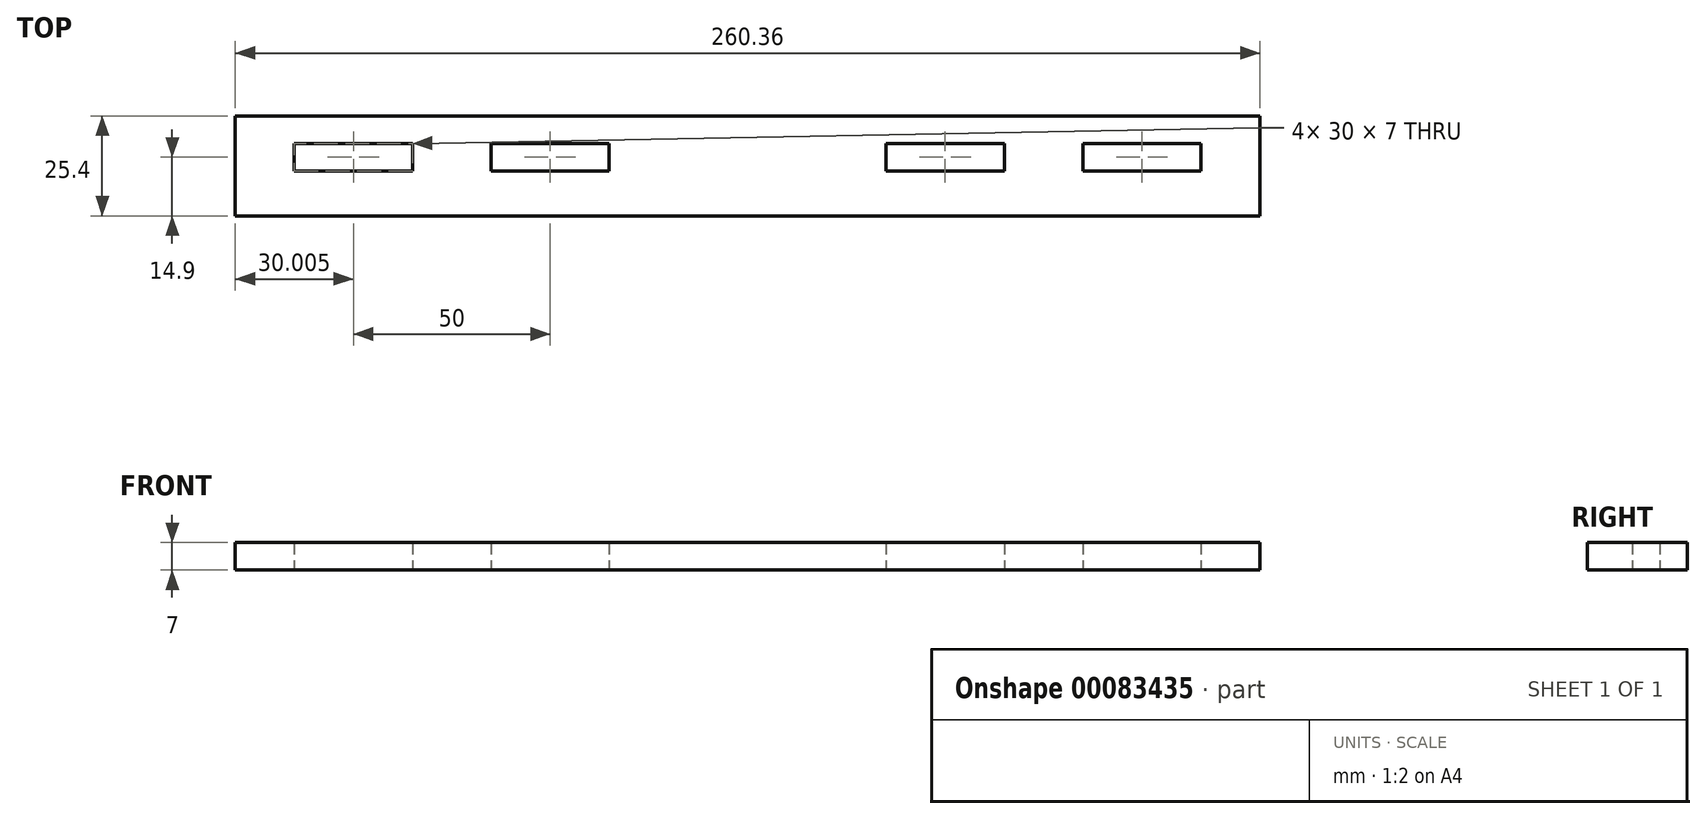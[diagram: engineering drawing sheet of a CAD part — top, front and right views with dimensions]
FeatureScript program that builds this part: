
annotation { "Feature Type Name" : "Feature", "Feature Type Description" : "" }
export const myFeature = defineFeature(function(context is Context, id is Id, definition is map)
    precondition{}
    {
        {
            var Q0;
            Q0=qCreatedBy(makeId("Top.planeOp"),FACE);
            var sketch = newSketch(context, id + "F0", { "sketchPlane" : qUnion([Q0])});
            skLineSegment(sketch, "E0.bottom", {"start": v(-130.18, 12.7) * mm, "end": v(130.18, 12.7) * mm});
            skLineSegment(sketch, "E0.top", {"start": v(-130.18, -12.7) * mm, "end": v(130.18, -12.7) * mm});
            skLineSegment(sketch, "E0.left", {"start": v(-130.18, 12.7) * mm, "end": v(-130.18, -12.7) * mm});
            skLineSegment(sketch, "E0.right", {"start": v(130.18, 12.7) * mm, "end": v(130.18, -12.7) * mm});
            skPoint(sketch, "E0.middle", {"position": v(0, 0) * mm});
            skLineSegment(sketch, "E1", {"start": v(-130.18, 5.7) * mm, "end": v(130.18, 5.7) * mm, "construction": true});
            skLineSegment(sketch, "E2.bottom", {"start": v(-115.18, 5.7) * mm, "end": v(-85.18, 5.7) * mm});
            skLineSegment(sketch, "E2.top", {"start": v(-115.18, -1.3) * mm, "end": v(-85.18, -1.3) * mm});
            skLineSegment(sketch, "E2.left", {"start": v(-115.18, 5.7) * mm, "end": v(-115.18, -1.3) * mm});
            skLineSegment(sketch, "E2.right", {"start": v(-85.18, 5.7) * mm, "end": v(-85.18, -1.3) * mm});
            skLineSegment(sketch, "E3.bottom", {"start": v(-65.18, 5.7) * mm, "end": v(-35.18, 5.7) * mm});
            skLineSegment(sketch, "E3.top", {"start": v(-65.18, -1.3) * mm, "end": v(-35.18, -1.3) * mm});
            skLineSegment(sketch, "E3.left", {"start": v(-65.18, 5.7) * mm, "end": v(-65.18, -1.3) * mm});
            skLineSegment(sketch, "E3.right", {"start": v(-35.18, 5.7) * mm, "end": v(-35.18, -1.3) * mm});
            skLineSegment(sketch, "E4.bottom", {"start": v(35.18, 5.7) * mm, "end": v(65.18, 5.7) * mm});
            skLineSegment(sketch, "E4.top", {"start": v(35.18, -1.3) * mm, "end": v(65.18, -1.3) * mm});
            skLineSegment(sketch, "E4.left", {"start": v(35.18, 5.7) * mm, "end": v(35.18, -1.3) * mm});
            skLineSegment(sketch, "E4.right", {"start": v(65.18, 5.7) * mm, "end": v(65.18, -1.3) * mm});
            skLineSegment(sketch, "E5.bottom", {"start": v(85.18, 5.7) * mm, "end": v(115.18, 5.7) * mm});
            skLineSegment(sketch, "E5.top", {"start": v(85.18, -1.3) * mm, "end": v(115.18, -1.3) * mm});
            skLineSegment(sketch, "E5.left", {"start": v(85.18, 5.7) * mm, "end": v(85.18, -1.3) * mm});
            skLineSegment(sketch, "E5.right", {"start": v(115.18, 5.7) * mm, "end": v(115.18, -1.3) * mm});
            skSolve(sketch);
        }
        {
            var Q0;
            Q0 = qSketchRegion(id + "F0", true);
            extrude(context, id + "F1", {"entities" : qUnion([Q0]), "depth" : 7 * mm});
        }
    });
